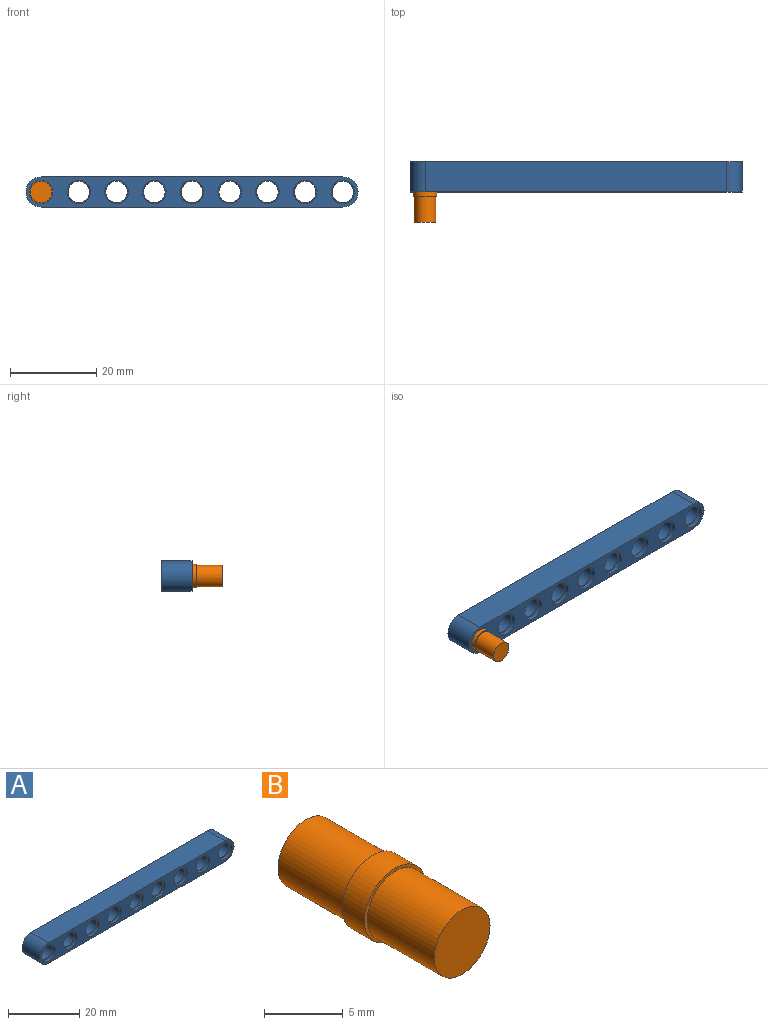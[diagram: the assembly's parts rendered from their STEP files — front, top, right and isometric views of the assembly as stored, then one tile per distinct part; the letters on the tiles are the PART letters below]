
ASSEMBLY  parts=2 mates=1
PART A: 51 faces, bbox 77x7x7 mm
  f0: cylinder r=2.5mm len=5mm, axis (0,1,0), area 78.5mm2, adj f32,f50
  f1: cylinder r=2.5mm len=5mm, axis (0,1,0), area 78.5mm2, adj f30,f48
  f2: cylinder r=2.5mm len=5mm, axis (0,1,0), area 78.5mm2, adj f28,f46
  f3: cylinder r=2.5mm len=5mm, axis (0,1,0), area 78.5mm2, adj f26,f44
  f4: cylinder r=2.5mm len=5mm, axis (0,1,0), area 78.5mm2, adj f24,f42
  f5: cylinder r=2.5mm len=5mm, axis (0,1,0), area 78.5mm2, adj f22,f40
  f6: cylinder r=2.5mm len=5mm, axis (0,1,0), area 78.5mm2, adj f20,f38
  f7: cylinder r=2.5mm len=5mm, axis (0,1,0), area 78.5mm2, adj f18,f36
  f8: cylinder r=2.5mm len=5mm, axis (0,1,0), area 78.5mm2, adj f16,f34
  f9: plane 70x7mm, normal (0,0,-1), area 490mm2, adj f10,f12,f13,f14
  f10: cylinder r=3.5mm len=7mm, axis (0,1,0), area 77mm2, adj f9,f11,f13,f14
  f11: plane 70x7mm, normal (0,0,1), area 490mm2, adj f10,f12,f13,f14
  f12: cylinder r=3.5mm len=7mm, axis (0,1,0), area 77mm2, adj f9,f11,f13,f14
  f13: plane 77x7mm, normal (0,-1,0), area 314.7mm2, adj f9,f10,f11,f12,f15,f17,f19,f21
  f14: plane 77x7mm, normal (0,1,0), area 314.7mm2, adj f9,f10,f11,f12,f33,f35,f37,f39
  f15: cylinder r=2.75mm len=5.5mm, axis (0,-1,0), area 17.3mm2, adj f13,f16
  f16: plane 5.5x5.5mm, normal (0,-1,0), area 4.1mm2, adj f8,f15
  f17: cylinder r=2.75mm len=5.5mm, axis (0,-1,0), area 17.3mm2, adj f13,f18
  f18: plane 5.5x5.5mm, normal (0,-1,0), area 4.1mm2, adj f7,f17
  f19: cylinder r=2.75mm len=5.5mm, axis (0,-1,0), area 17.3mm2, adj f13,f20
  f20: plane 5.5x5.5mm, normal (0,-1,0), area 4.1mm2, adj f6,f19
  f21: cylinder r=2.75mm len=5.5mm, axis (0,-1,0), area 17.3mm2, adj f13,f22
  f22: plane 5.5x5.5mm, normal (0,-1,0), area 4.1mm2, adj f5,f21
  f23: cylinder r=2.75mm len=5.5mm, axis (0,-1,0), area 17.3mm2, adj f13,f24
  f24: plane 5.5x5.5mm, normal (0,-1,0), area 4.1mm2, adj f4,f23
  f25: cylinder r=2.75mm len=5.5mm, axis (0,-1,0), area 17.3mm2, adj f13,f26
  f26: plane 5.5x5.5mm, normal (0,-1,0), area 4.1mm2, adj f3,f25
  f27: cylinder r=2.75mm len=5.5mm, axis (0,-1,0), area 17.3mm2, adj f13,f28
  f28: plane 5.5x5.5mm, normal (0,-1,0), area 4.1mm2, adj f2,f27
  f29: cylinder r=2.75mm len=5.5mm, axis (0,-1,0), area 17.3mm2, adj f13,f30
  f30: plane 5.5x5.5mm, normal (0,-1,0), area 4.1mm2, adj f1,f29
  f31: cylinder r=2.75mm len=5.5mm, axis (0,-1,0), area 17.3mm2, adj f13,f32
  f32: plane 5.5x5.5mm, normal (0,-1,0), area 4.1mm2, adj f0,f31
  f33: cylinder r=2.75mm len=5.5mm, axis (0,1,0), area 17.3mm2, adj f14,f34
  f34: plane 5.5x5.5mm, normal (0,1,0), area 4.1mm2, adj f8,f33
  f35: cylinder r=2.75mm len=5.5mm, axis (0,1,0), area 17.3mm2, adj f14,f36
  f36: plane 5.5x5.5mm, normal (0,1,0), area 4.1mm2, adj f7,f35
  f37: cylinder r=2.75mm len=5.5mm, axis (0,1,0), area 17.3mm2, adj f14,f38
  f38: plane 5.5x5.5mm, normal (0,1,0), area 4.1mm2, adj f6,f37
  f39: cylinder r=2.75mm len=5.5mm, axis (0,1,0), area 17.3mm2, adj f14,f40
  f40: plane 5.5x5.5mm, normal (0,1,0), area 4.1mm2, adj f5,f39
  f41: cylinder r=2.75mm len=5.5mm, axis (0,1,0), area 17.3mm2, adj f14,f42
  f42: plane 5.5x5.5mm, normal (0,1,0), area 4.1mm2, adj f4,f41
  f43: cylinder r=2.75mm len=5.5mm, axis (0,1,0), area 17.3mm2, adj f14,f44
  f44: plane 5.5x5.5mm, normal (0,1,0), area 4.1mm2, adj f3,f43
  f45: cylinder r=2.75mm len=5.5mm, axis (0,1,0), area 17.3mm2, adj f14,f46
  f46: plane 5.5x5.5mm, normal (0,1,0), area 4.1mm2, adj f2,f45
  f47: cylinder r=2.75mm len=5.5mm, axis (0,1,0), area 17.3mm2, adj f14,f48
  f48: plane 5.5x5.5mm, normal (0,1,0), area 4.1mm2, adj f1,f47
  f49: cylinder r=2.75mm len=5.5mm, axis (0,1,0), area 17.3mm2, adj f14,f50
  f50: plane 5.5x5.5mm, normal (0,1,0), area 4.1mm2, adj f0,f49
PART B: 7 faces, bbox 5.5x14x5.5 mm
  f0: cylinder r=2.75mm len=5.5mm, axis (0,1,0), area 34.6mm2, adj f2,f5
  f1: cylinder r=2.5mm len=6mm, axis (0,-1,0), area 94.2mm2, adj f2,f3
  f2: plane 5.5x5.5mm, normal (0,-1,0), area 4.1mm2, adj f0,f1
  f3: plane 5x5mm, normal (0,-1,0), area 19.6mm2, adj f1
  f4: cylinder r=2.5mm len=6mm, axis (0,1,0), area 94.2mm2, adj f5,f6
  f5: plane 5.5x5.5mm, normal (0,1,0), area 4.1mm2, adj f0,f4
  f6: plane 5x5mm, normal (0,1,0), area 19.6mm2, adj f4
PLACE A t=(20.41,-5.01,-5.38)mm
PLACE B t=(-14.59,-12.01,-5.38)mm
MATE fastened A.f0 <-> B.f0  axis (0,-1,0) through (-14.59,-11.01,-5.38)mm
